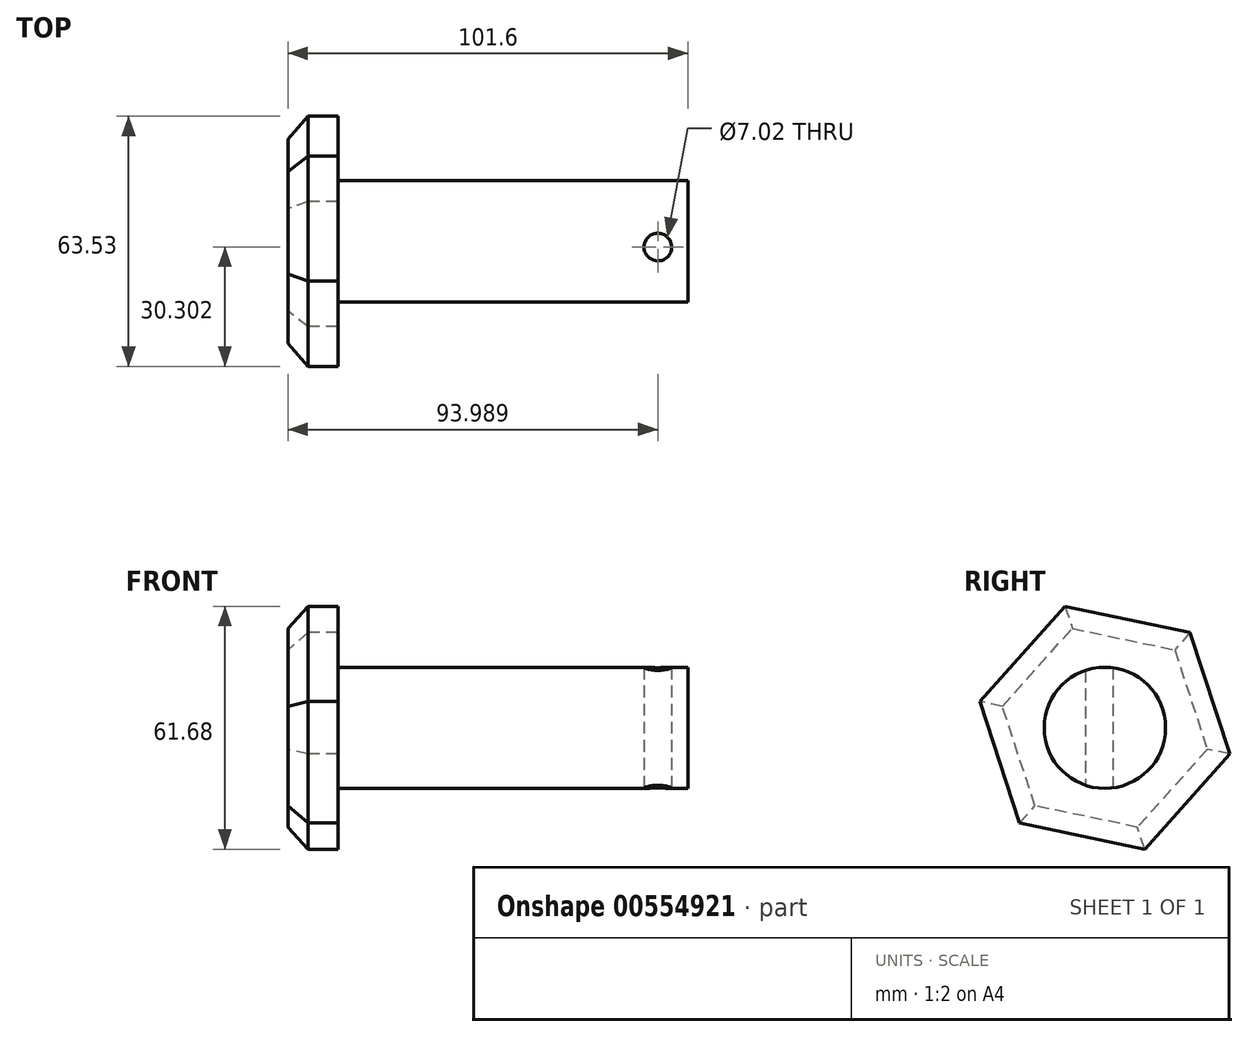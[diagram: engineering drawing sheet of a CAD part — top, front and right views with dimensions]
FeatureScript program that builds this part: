
annotation { "Feature Type Name" : "Feature", "Feature Type Description" : "" }
export const myFeature = defineFeature(function(context is Context, id is Id, definition is map)
    precondition{}
    {
        {
            var Q0;
            Q0=qCreatedBy(makeId("Right.planeOp"),FACE);
            var sketch = newSketch(context, id + "F0", { "sketchPlane" : qUnion([Q0])});
            skCircle(sketch, "E0", {"center": v(0.24, 1.46) * mm, "radius": 15.4 * mm});
            skSolve(sketch);
        }
        {
            var Q0;
            Q0=makeQuery(id+"F0.imprint","IMPRINT",FACE,{"disambiguationData":[TD([[makeQuery(id+"F0.imprint","IMPRINT",EDGE,{"derivedFrom":sQuery(id+"F0.wireOp",EDGE,"E0")}),1.0]])]});
            extrude(context, id + "F1", {"entities" : qUnion([Q0]), "depth" : 101.6 * mm, "offsetDistance" : 25.4 * mm});
        }
        {
            var Q0;
            Q0=makeQuery(id+"F1.opExtrude","CAP_FACE",FACE,{"disambiguationData":[OSD([sQuery(id+"F0.wireOp",EDGE,"E0")])],"isStart":true});
            var sketch = newSketch(context, id + "F2", { "sketchPlane" : qUnion([Q0])});
            skCircle(sketch, "E1.cCircle", {"center": v(-0.24, 1.46) * mm, "radius": 28.1 * mm, "construction": true});
            skLineSegment(sketch, "E1.0", {"start": v(9.87, 32.3) * mm, "end": v(31.52, 8.12) * mm});
            skLineSegment(sketch, "E1.1", {"start": v(31.52, 8.12) * mm, "end": v(21.4, -22.72) * mm});
            skLineSegment(sketch, "E1.2", {"start": v(21.4, -22.72) * mm, "end": v(-10.36, -29.38) * mm});
            skLineSegment(sketch, "E1.3", {"start": v(-10.36, -29.38) * mm, "end": v(-32, -5.2) * mm});
            skLineSegment(sketch, "E1.4", {"start": v(-32, -5.2) * mm, "end": v(-21.9, 25.64) * mm});
            skLineSegment(sketch, "E1.5", {"start": v(-21.9, 25.64) * mm, "end": v(9.87, 32.3) * mm});
            skPoint(sketch, "E1.0.midPoint", {"position": v(20.7, 20.21) * mm});
            skSolve(sketch);
        }
        {
            var Q0;
            Q0=makeQuery(id+"F2.imprint","IMPRINT",FACE,{"disambiguationData":[TD([[makeQuery(id+"F2.imprint","IMPRINT",EDGE,{"derivedFrom":sQuery(id+"F2.wireOp",EDGE,"E1.0")}),-1.0]])]});
            extrude(context, id + "F3", {"entities" : qUnion([Q0]), "operationType" : NewBodyOperationType.ADD, "oppositeDirection" : true, "depth" : 12.7 * mm, "offsetDistance" : 25.4 * mm});
        }
        {
            var Q0;
            Q0=makeQuery(id+"F3.opExtrude","CAP_EDGE",EDGE,{"disambiguationData":[OSD([sQuery(id+"F2.wireOp",EDGE,"E1.4")])],"isStart":true});
            var Q1;
            Q1=makeQuery(id+"F3.opExtrude","CAP_EDGE",EDGE,{"disambiguationData":[OSD([sQuery(id+"F2.wireOp",EDGE,"E1.5")])],"isStart":true});
            var Q2;
            Q2=makeQuery(id+"F3.opExtrude","CAP_EDGE",EDGE,{"disambiguationData":[OSD([sQuery(id+"F2.wireOp",EDGE,"E1.0")])],"isStart":true});
            var Q3;
            Q3=makeQuery(id+"F3.opExtrude","CAP_EDGE",EDGE,{"disambiguationData":[OSD([sQuery(id+"F2.wireOp",EDGE,"E1.1")])],"isStart":true});
            var Q4;
            Q4=makeQuery(id+"F3.opExtrude","CAP_EDGE",EDGE,{"disambiguationData":[OSD([sQuery(id+"F2.wireOp",EDGE,"E1.2")])],"isStart":true});
            var Q5;
            Q5=makeQuery(id+"F3.opExtrude","CAP_EDGE",EDGE,{"disambiguationData":[OSD([sQuery(id+"F2.wireOp",EDGE,"E1.3")])],"isStart":true});
            chamfer(context, id + "F4", {"entities" : qUnion([Q0, Q1, Q2, Q3, Q4, Q5]), "width" : 5.08 * mm, "tangentPropagation" : true});
        }
        {
            var Q0;
            Q0=qCreatedBy(makeId("Top.planeOp"),FACE);
            var sketch = newSketch(context, id + "F5", { "sketchPlane" : qUnion([Q0])});
            skCircle(sketch, "E2", {"center": v(93.99, -1.22) * mm, "radius": 3.51 * mm});
            skSolve(sketch);
        }
        {
            var Q0;
            Q0 = qSketchRegion(id + "F5", true);
            extrude(context, id + "F6", {"entities" : qUnion([Q0]), "operationType" : NewBodyOperationType.REMOVE, "endBound" : BoundingType.THROUGH_ALL, "depth" : 25.4 * mm, "offsetDistance" : 25.4 * mm, "hasSecondDirection" : true, "secondDirectionBound" : SecondDirectionBoundingType.THROUGH_ALL, "secondDirectionOppositeDirection" : true, "secondDirectionDepth" : 25.4 * mm});
        }
    });
